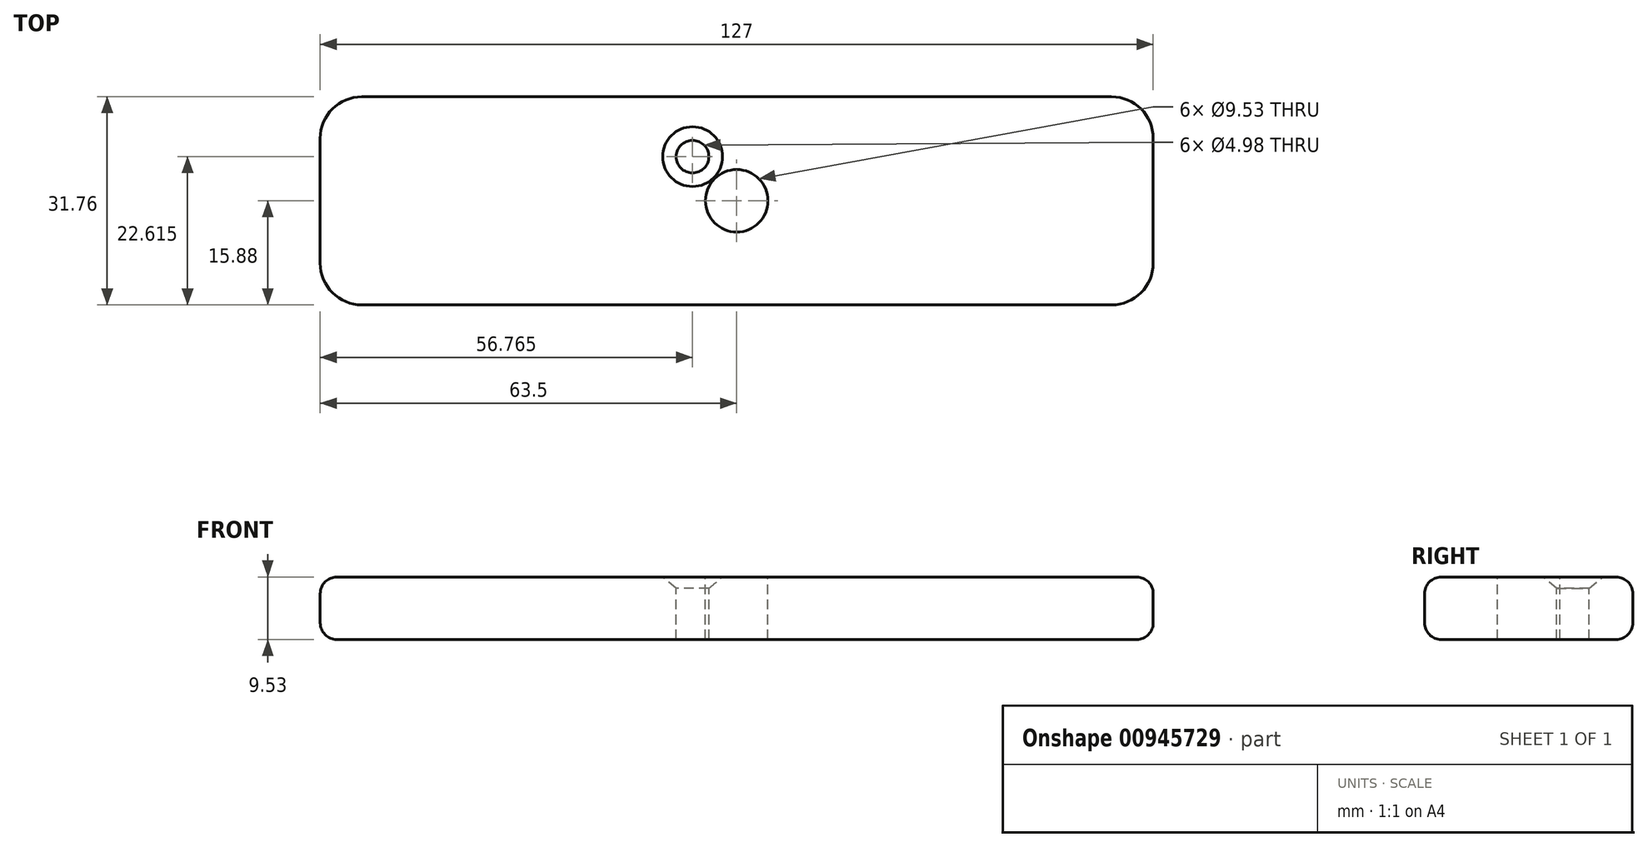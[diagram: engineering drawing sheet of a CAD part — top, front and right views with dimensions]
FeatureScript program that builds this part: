
annotation { "Feature Type Name" : "Feature", "Feature Type Description" : "" }
export const myFeature = defineFeature(function(context is Context, id is Id, definition is map)
    precondition{}
    {
        {
            var Q0;
            Q0=qCreatedBy(makeId("Top.planeOp"),FACE);
            var sketch = newSketch(context, id + "F0", { "sketchPlane" : qUnion([Q0])});
            skLineSegment(sketch, "E0.bottom", {"start": v(57.15, -15.88) * mm, "end": v(-57.15, -15.88) * mm});
            skLineSegment(sketch, "E0.top", {"start": v(57.15, 15.87) * mm, "end": v(-57.15, 15.87) * mm});
            skLineSegment(sketch, "E0.left", {"start": v(63.5, -9.53) * mm, "end": v(63.5, 9.52) * mm});
            skLineSegment(sketch, "E0.right", {"start": v(-63.5, -9.53) * mm, "end": v(-63.5, 9.52) * mm});
            skPoint(sketch, "E0.middle", {"position": v(0, 0) * mm});
            skPoint(sketch, "E1.visualSharp", {"position": v(-63.5, 15.87) * mm});
            skArc(sketch, "E1.filletArc", {"start": v(-57.15, 15.87) * mm, "mid": v(-61.64, 14.02) * mm, "end": v(-63.5, 9.52) * mm});
            skPoint(sketch, "E2.visualSharp", {"position": v(-63.5, -15.88) * mm});
            skArc(sketch, "E2.filletArc", {"start": v(-63.5, -9.53) * mm, "mid": v(-61.64, -14.02) * mm, "end": v(-57.15, -15.88) * mm});
            skPoint(sketch, "E3.visualSharp", {"position": v(63.5, -15.88) * mm});
            skArc(sketch, "E3.filletArc", {"start": v(57.15, -15.88) * mm, "mid": v(61.64, -14.02) * mm, "end": v(63.5, -9.53) * mm});
            skPoint(sketch, "E4.visualSharp", {"position": v(63.5, 15.87) * mm});
            skArc(sketch, "E4.filletArc", {"start": v(63.5, 9.52) * mm, "mid": v(61.64, 14.02) * mm, "end": v(57.15, 15.87) * mm});
            skSolve(sketch);
        }
        {
            var Q0;
            Q0 = qSketchRegion(id + "F0", true);
            extrude(context, id + "F1", {"entities" : qUnion([Q0]), "depth" : 9.52 * mm, "offsetDistance" : 25.4 * mm});
        }
        {
            var Q0;
            Q0=makeQuery(id+"F1.opExtrude","CAP_FACE",FACE,{"disambiguationData":[OSD([sQuery(id+"F0.wireOp",EDGE,"E0.bottom"),sQuery(id+"F0.wireOp",EDGE,"E0.top"),sQuery(id+"F0.wireOp",EDGE,"E0.left"),sQuery(id+"F0.wireOp",EDGE,"E0.right"),sQuery(id+"F0.wireOp",EDGE,"E1.filletArc"),sQuery(id+"F0.wireOp",EDGE,"E2.filletArc"),sQuery(id+"F0.wireOp",EDGE,"E3.filletArc"),sQuery(id+"F0.wireOp",EDGE,"E4.filletArc")])],"isStart":false});
            var Q1;
            Q1=makeQuery(id+"F1.opExtrude","CAP_FACE",FACE,{"disambiguationData":[OSD([sQuery(id+"F0.wireOp",EDGE,"E0.bottom"),sQuery(id+"F0.wireOp",EDGE,"E0.top"),sQuery(id+"F0.wireOp",EDGE,"E0.left"),sQuery(id+"F0.wireOp",EDGE,"E0.right"),sQuery(id+"F0.wireOp",EDGE,"E1.filletArc"),sQuery(id+"F0.wireOp",EDGE,"E2.filletArc"),sQuery(id+"F0.wireOp",EDGE,"E3.filletArc"),sQuery(id+"F0.wireOp",EDGE,"E4.filletArc")])],"isStart":true});
            fillet(context, id + "F2", {"entities" : qUnion([Q0, Q1]), "radius" : 2.54 * mm, "tangentPropagation" : true, "allowEdgeOverflow" : false});
        }
        {
            var Q0;
            Q0=makeQuery(id+"F1.opExtrude","CAP_FACE",FACE,{"disambiguationData":[OSD([sQuery(id+"F0.wireOp",EDGE,"E0.bottom"),sQuery(id+"F0.wireOp",EDGE,"E0.top"),sQuery(id+"F0.wireOp",EDGE,"E0.left"),sQuery(id+"F0.wireOp",EDGE,"E0.right"),sQuery(id+"F0.wireOp",EDGE,"E1.filletArc"),sQuery(id+"F0.wireOp",EDGE,"E2.filletArc"),sQuery(id+"F0.wireOp",EDGE,"E3.filletArc"),sQuery(id+"F0.wireOp",EDGE,"E4.filletArc")])],"isStart":false});
            var sketch = newSketch(context, id + "F3", { "sketchPlane" : qUnion([Q0])});
            skCircle(sketch, "E5", {"center": v(0, 0) * mm, "radius": 4.76 * mm});
            skSolve(sketch);
        }
        {
            var Q0;
            Q0 = qSketchRegion(id + "F3", true);
            extrude(context, id + "F4", {"entities" : qUnion([Q0]), "operationType" : NewBodyOperationType.REMOVE, "oppositeDirection" : true, "depth" : 25.4 * mm, "offsetDistance" : 25.4 * mm});
        }
        {
            var Q0;
            Q0=makeQuery(id+"F1.opExtrude","CAP_FACE",FACE,{"disambiguationData":[OSD([sQuery(id+"F0.wireOp",EDGE,"E0.bottom"),sQuery(id+"F0.wireOp",EDGE,"E0.top"),sQuery(id+"F0.wireOp",EDGE,"E0.left"),sQuery(id+"F0.wireOp",EDGE,"E0.right"),sQuery(id+"F0.wireOp",EDGE,"E1.filletArc"),sQuery(id+"F0.wireOp",EDGE,"E2.filletArc"),sQuery(id+"F0.wireOp",EDGE,"E3.filletArc"),sQuery(id+"F0.wireOp",EDGE,"E4.filletArc")])],"isStart":false});
            var sketch = newSketch(context, id + "F5", { "sketchPlane" : qUnion([Q0])});
            skPoint(sketch, "E6", {"position": v(-6.74, 6.74) * mm});
            skLineSegment(sketch, "E7", {"start": v(-6.74, 6.74) * mm, "end": v(0, 0) * mm, "construction": true});
            skSolve(sketch);
        }
        {
            var Q0;
            Q0=sQuery(id+"F5.wireOp",VERTEX,"E6");
            var Q1;
            Q1=makeQuery(id+"F1.opExtrude","SWEPT_BODY",BODY,{"disambiguationData":[OSD([sQuery(id+"F0.wireOp",EDGE,"E0.bottom"),sQuery(id+"F0.wireOp",EDGE,"E0.top"),sQuery(id+"F0.wireOp",EDGE,"E0.left"),sQuery(id+"F0.wireOp",EDGE,"E0.right"),sQuery(id+"F0.wireOp",EDGE,"E1.filletArc"),sQuery(id+"F0.wireOp",EDGE,"E2.filletArc"),sQuery(id+"F0.wireOp",EDGE,"E3.filletArc"),sQuery(id+"F0.wireOp",EDGE,"E4.filletArc")])]});
            hole(context, id + "F6", {"style" : HoleStyle.C_SINK, "endStyle" : HoleEndStyle.THROUGH, "holeDiameter" : 4.98 * mm, "cSinkDiameter" : 9.12 * mm, "cSinkAngle" : 100 * degree, "majorDiameter" : 6.35 * mm, "isTappedThrough" : true, "tappedDepth" : 12.7 * mm, "tapClearance" : 3, "startFromSketch" : true, "locations" : qUnion([Q0]), "scope" : qUnion([Q1])});
        }
    });
